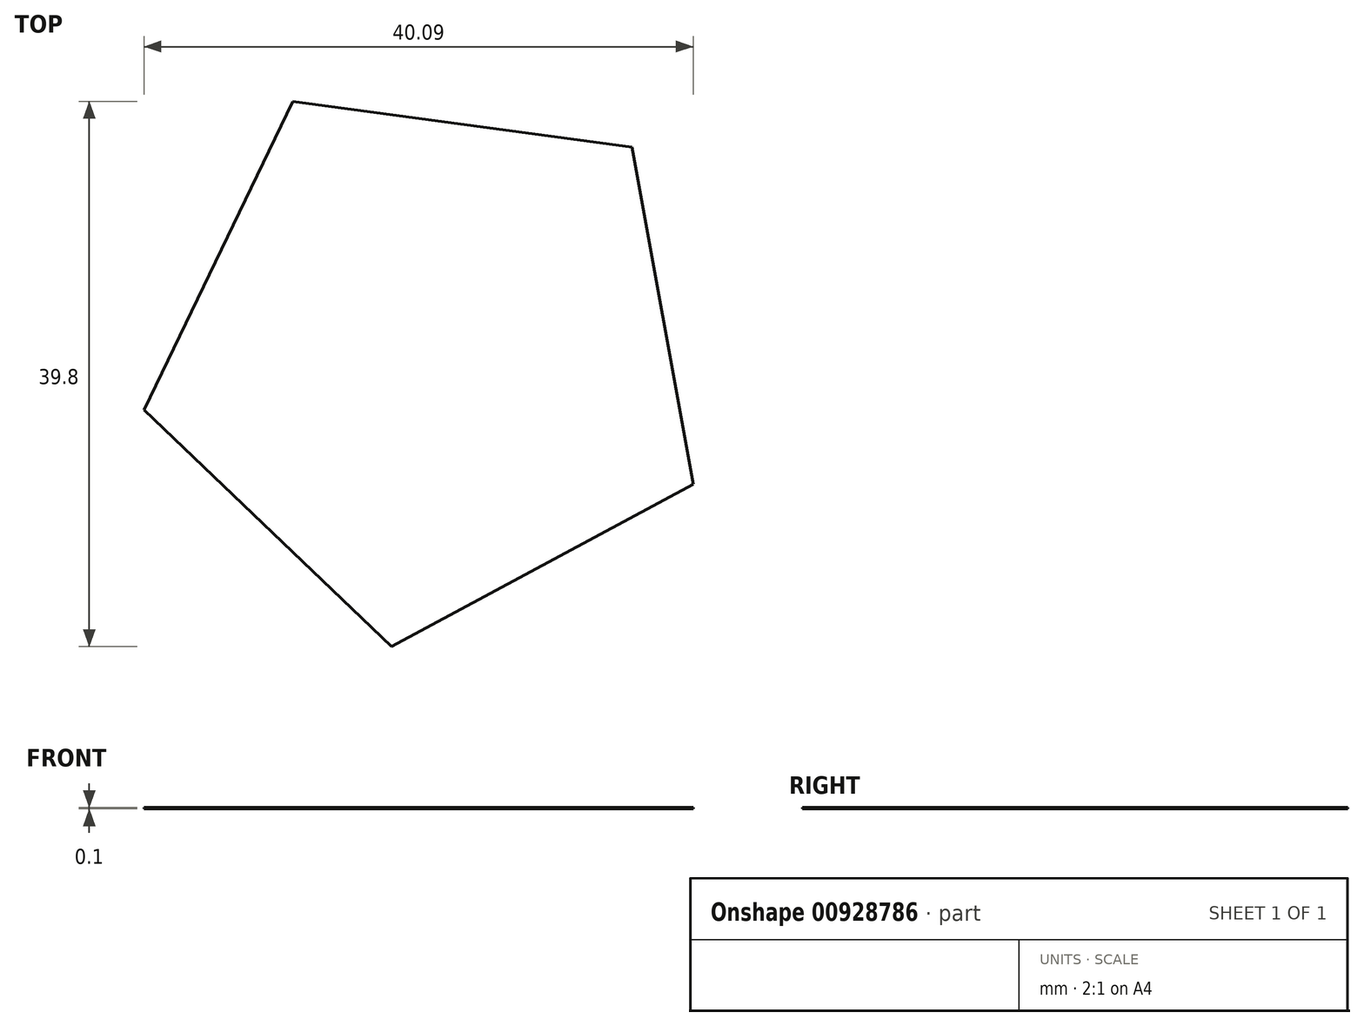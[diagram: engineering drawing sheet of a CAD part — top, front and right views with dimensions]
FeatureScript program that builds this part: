
annotation { "Feature Type Name" : "Feature", "Feature Type Description" : "" }
export const myFeature = defineFeature(function(context is Context, id is Id, definition is map)
    precondition{}
    {
        {
            var Q0;
            Q0=qCreatedBy(makeId("Top.planeOp"),FACE);
            var sketch = newSketch(context, id + "F0", { "sketchPlane" : qUnion([Q0])});
            skCircle(sketch, "E0.cCircle", {"center": v(0, 0) * mm, "radius": 17.2 * mm, "construction": true});
            skLineSegment(sketch, "E0.0", {"start": v(19.16, -9.23) * mm, "end": v(-2.86, -21.07) * mm});
            skLineSegment(sketch, "E0.1", {"start": v(-2.86, -21.07) * mm, "end": v(-20.93, -3.8) * mm});
            skLineSegment(sketch, "E0.2", {"start": v(-20.93, -3.8) * mm, "end": v(-10.07, 18.73) * mm});
            skLineSegment(sketch, "E0.3", {"start": v(-10.07, 18.73) * mm, "end": v(14.7, 15.37) * mm});
            skLineSegment(sketch, "E0.4", {"start": v(14.7, 15.37) * mm, "end": v(19.16, -9.23) * mm});
            skPoint(sketch, "E0.0.midPoint", {"position": v(8.15, -15.15) * mm});
            skSolve(sketch);
        }
        {
            var Q0;
            Q0=makeQuery(id+"F0.imprint","IMPRINT",FACE,{"disambiguationData":[TD([[makeQuery(id+"F0.imprint","IMPRINT",EDGE,{"derivedFrom":sQuery(id+"F0.wireOp",EDGE,"E0.0")}),-1.0]])]});
            extrude(context, id + "F1", {"entities" : qUnion([Q0]), "depth" : 0.1 * mm, "offsetDistance" : 25 * mm});
        }
    });
